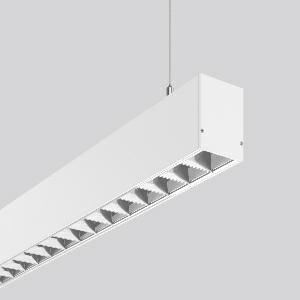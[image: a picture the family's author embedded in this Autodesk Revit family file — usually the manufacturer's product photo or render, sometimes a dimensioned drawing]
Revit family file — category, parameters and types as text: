
# Revit family: less_is_more_50_312343_002_87ee
name_source: partatom
category: Lighting Fixtures
units: mm (PartAtom-declared; Revit-internal decimal feet)

## family parameters
Cut with Voids When Loaded = No
Host = Face
Light Source = No
Part Type = Normal
Room Calculation Point = No
Round Connector Dimension = Use Diameter
Shared = No

## types (1)
- LESS IS MORE 50 (1 x LED Modul 830, 6400 lm, 3000)
    Apparent Load = 58 VA
    CIE Flux Codes = 95 100 100 63 100
    Color Rendering = 80
    Color Temperature = 3000
    Default Elevation = 1800 mm
    Description = Series: LESS IS MORE 50
Linear pendant luminaire for aesthetically sophisticated lighting. Housing: extruded aluminium profile, powder-coated. End cap aluminium powder-coated. Canopy made of aluminium, powder-coated. Alea optical system: Reflector structure (ABS, Aluminium-coated, highly polished) with integrated diffuser made of non-yellowing plastic (PMMA) opal for glare-free light at the workstation (screen-compliant according to EN 12464-1). Direct 65%, indirect 35% light emission. Suitable for pendant. 2-point steel cable suspension freely positionable and infinitely height-adjustable. Special lengths available on request. LED unit with integrated converter interchangeable and removable. Suitable for through-wiring. With sensors or as a safety luminaire on request. 
Colour: traffic white, matt (RAL 9016)
Length: 1407 mm
Width: 57 mm
Height: 75 mm
Suspension length: 2000 mm
Lamp: LED
Socket: without socket
Colour temperature: 3000K
Colour rendering index (CRI): 80
Light source: LED
Socket lamp2: Without base
Colour temperature: 3000K
System power: 58 W
Rated luminous flux: 6400 lm
Luminous efficiency: 110 lm/W
Control gear: Regulated power supply
Control gear: Regulated power supply
Protection class: I
Type of protection: IP 20
    Height = 75 mm
    Lamp = 1 x LED Modul 830
    Lamp Light Flux = 6400 lm
    Lamp count = 1
    Length = 1407 mm
    Lifetime = 50000 h
    Luminous efficacy = 110 lm/W
    Manufacturer = RZB
    ModVariant = No
    Model = 312343.002
    Mounting Place = Ceiling
    Mounting Type = Pendant
    Number of Poles = 1
    OnlyDefault = Yes
    Power Factor = 1
    Product Name = LESS IS MORE 50
    Product group = Pendant LED linear luminaires
    ProductGroupID = 907
    Protection Class = Protection class I
    Protection Degree = IP 20
    RLX_Detail_Level = 1
    RLX_Emergency_Light_Flux = 0 lm
    RLX_Emergency_Type = 0
    RLX_Emergency_Type_DB = No
    RlxData = <blob elided: 37445 chars, md5=28c4dc00>
    Socket = socket
    Standby Power = 0 W
    System Light Flux = 6400 lm
    System Power = 58 W
    Type Comments = Product without accessories
    Type Image = 312342.002.jpg
    URL = http://relux.com
    VarID = ---
    Voltage = 230 V
    Voltage Range = 220-240 V
    Weight = 0.00 kg
    Width = 57 mm

## geometry (parser evidence)
native form markers: Blend x4, Sweep x12
no freeform markers — native parametric forms only
